# Revit family: AB2LED
name_source: partatom
category: Lighting Fixtures
revit_build: Autodesk Revit 2014 (Build: 20130308_1515(x64)
units: mm (PartAtom-declared; Revit-internal decimal feet)

## types (1)
- AB2LED
    Apparent Load = 0 VA
    Assembly Code = D5020200
    Back Plate = Hubbell - Black
    Color Filter = 16777215
    Default Elevation = 48.000"
    Description = 2'' LED Adjustable Aim From Below
    Dimming Lamp Color Temperature Shift = <None>
    Emit Shape Visible in Rendering = No
    Emit from Circle Diameter = 2.500"
    Housing = Hubbell - Steel
    Input Power = 14 W
    Lamp = LED
    Load Classification = Lighting
    Manufacturer = Prescolite
    Model = AB2LED
    Photometric Web File = AB2LED-2AB9LED7L30K8WFL45.IES
    Power Factor = 1
    Product Documentation Link = https://hubbellcdn.com
    Product Link = https://www.hubbell.com
    Reflector = Aluminum - Hubbell
    Tilt Angle = -90.00°
    URL = http://www.prescolite.com
    Voltage = 120 V
    Wattage Comments = 13.8W to 22.4 W

## geometry (parser evidence)
native form markers: Blend x4, Sweep x1
no freeform markers — native parametric forms only
